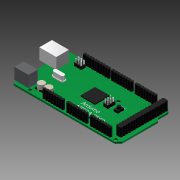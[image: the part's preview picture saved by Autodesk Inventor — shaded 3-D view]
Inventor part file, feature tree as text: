
AUTODESK INVENTOR PART (.ipt)
format: ipt  version: 2012 (Build 160160000, 160)  size: 1,303,040 bytes
history: native  units: mm (DEFAULTED — no unit token found)
features: extrude x16, sketch x8, plane x1
ambient origin geometry x8: Origin, YZ Plane, XZ Plane, XY Plane, X Axis, Y Axis, Z Axis, Center Point
bodies: Solid1 (feature_tree)
feature tree (25):
  extrude  "PCB"  Depth=53.339919mm
  sketch  "Sketch3"  dims[d53=101.599932mm d54=1.6mm d55=0.0mm]
  extrude  "Socket"  Depth=1.6mm TaperAngle=0.0deg
  extrude  "Atmel2560"  Depth=15.240007mm
  extrude  "Quarz1"  Depth=90.169956mm
  extrude  "Quarz2"  Depth=2.539965mm
  extrude  "Extrusion7"  Depth=7.619995mm
  extrude  "Extrusion8"  Depth=98.059928mm
  extrude  "Switch1"  TaperAngle=45.0deg  [1 undecoded]
  extrude  "Switch2"  Depth=2.539987mm
  extrude  "Pins1"  Depth=2.540017mm
  extrude  "Pins2"  Depth=1.269977mm
  extrude  "Power"  Depth=12.699981mm
  extrude  "Power2"  Depth=8.3mm TaperAngle=0.0deg
  extrude  "Text"  Depth=2.5mm TaperAngle=0.0deg
  plane  "Work Plane1"
  extrude  "Extrusion15"  Depth=1.0mm TaperAngle=0.0deg
  extrude  "Extrusion16"  Depth=1.0mm TaperAngle=0.0deg
  sketch  "Sketch1"  dims[d51=3.199998mm d52=53.339919mm]
  sketch  "Sketch4"  dims[d56=13.970007mm d57=15.240007mm]
  sketch  "Sketch5"  dims[d58=66.039973mm d59=90.169956mm]
  sketch  "Sketch6"  dims[d60=96.519952mm d61=2.539965mm]
  sketch  "Sketch7"  dims[d62=50.799932mm d63=7.619995mm]
  sketch  "Sketch8"  dims[d64=27.939948mm d65=98.059928mm]
  sketch  "Sketch9"  dims[d66=1.0mm d67=45.0deg d68=2.539987mm d69=2.540017mm d73=1.269977mm d74=12.699981mm d77=8.3mm d78=0.0mm d79=2.5mm d80=0.0mm d81=1.0mm d82=0.0mm d83=1.0mm d84=0.0mm d85=5.0mm d86=0.0mm d87=5.0mm d88=0.0mm d89=1.0mm d90=0.0mm d91=2.0mm d92=0.0mm d93=4.0mm d94=0.0mm d95=1.0mm d96=1.0mm d97=2.5mm d98=1.29mm d99=1.29mm d100=2.5mm d101=1.29mm d102=3.5mm d103=0.0mm d104=13.5mm d105=9.0mm d106=3.3mm d107=1.8mm d108=11.0mm d109=0.0mm d110=5.0mm d111=10.0mm d112=0.0mm d113=19.0mm d114=52.0mm d115=0.1mm d116=0.0mm d117=16.3mm d118=0.0mm d119=5.0mm d120=0.0mm]
note: 1 required parameter value undecoded (feature->parameter linkage not recoverable at this tier; creation-order binding heuristic only, values carry confidence <= 0.55)
